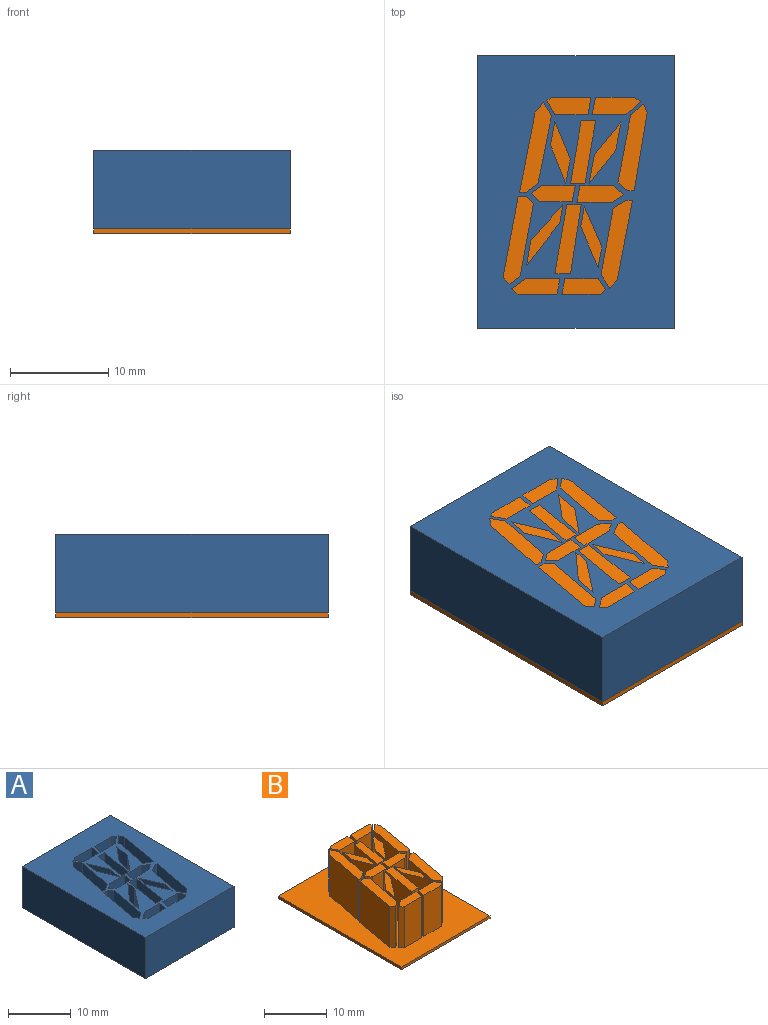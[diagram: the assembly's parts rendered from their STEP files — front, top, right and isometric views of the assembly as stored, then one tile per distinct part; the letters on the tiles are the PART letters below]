
ASSEMBLY  parts=2 mates=1
PART A: 84 faces, bbox 20x27.7x8 mm
  f0: plane 8x3.38mm, normal (0,1,0), area 27mm2, adj f1,f81,f82,f83
  f1: plane 8x1.47mm, normal (0.87,0.49,0), area 13.5mm2, adj f0,f2,f82,f83
  f2: plane 8x0.6mm, normal (0.49,-0.87,0), area 5.4mm2, adj f1,f3,f82,f83
  f3: plane 8x3.88mm, normal (0,-1,0), area 31mm2, adj f2,f81,f82,f83
  f4: plane 8x3.46mm, normal (0,1,0), area 27.6mm2, adj f5,f65,f82,f83
  f5: plane 8x1.8mm, normal (0.98,-0.2,0), area 14.7mm2, adj f4,f6,f82,f83
  f6: plane 8x3.86mm, normal (0,-1,0), area 30.9mm2, adj f5,f7,f82,f83
  f7: plane 8x0.69mm, normal (-0.51,-0.86,0), area 6.5mm2, adj f6,f65,f82,f83
  f8: plane 8x6.88mm, normal (0.98,-0.18,0), area 56mm2, adj f9,f66,f82,f83
  f9: plane 8x1.33mm, normal (0.64,-0.77,0), area 13.8mm2, adj f8,f10,f82,f83
  f10: plane 8x0.86mm, normal (-0.92,-0.38,0), area 7.4mm2, adj f9,f11,f82,f83
  f11: plane 8x7.96mm, normal (-0.99,0.16,0), area 64.6mm2, adj f10,f12,f82,f83
  f12: plane 8x0.66mm, normal (0,1,0), area 5.3mm2, adj f11,f66,f82,f83
  f13: plane 8x1.39mm, normal (0.84,0.54,0), area 13.3mm2, adj f14,f67,f82,f83
  f14: plane 8x6.77mm, normal (0.98,-0.18,0), area 55.1mm2, adj f13,f15,f82,f83
  f15: plane 8x1.39mm, normal (0.51,-0.86,0), area 12.8mm2, adj f14,f16,f82,f83
  f16: plane 8x0.57mm, normal (0,-1,0), area 4.6mm2, adj f15,f17,f82,f83
  f17: plane 8.08x8mm, normal (-0.98,0.19,0), area 65.8mm2, adj f16,f67,f82,f83
  f18: plane 8x3.87mm, normal (0,1,0), area 31mm2, adj f19,f68,f82,f83
  f19: plane 8x1.61mm, normal (0.98,-0.18,0), area 13.1mm2, adj f18,f20,f82,f83
  f20: plane 8x3.39mm, normal (0,-1,0), area 27.1mm2, adj f19,f21,f82,f83
  f21: plane 8x1.15mm, normal (-0.84,-0.54,0), area 11mm2, adj f20,f68,f82,f83
  f22: plane 8x1.6mm, normal (-0.98,0.19,0), area 13.1mm2, adj f23,f69,f82,f83
  f23: plane 8x3.94mm, normal (0,1,0), area 31.5mm2, adj f22,f24,f82,f83
  f24: plane 8x0.64mm, normal (0.65,0.76,0), area 6.7mm2, adj f23,f25,f82,f83
  f25: plane 8x1.43mm, normal (0.59,-0.81,0), area 14.2mm2, adj f24,f69,f82,f83
  f26: plane 8x1.13mm, normal (-0.63,0.78,0), area 11.6mm2, adj f27,f70,f82,f83
  f27: plane 8x0.69mm, normal (0.74,0.67,0), area 7.4mm2, adj f26,f28,f82,f83
  f28: plane 8.3x8mm, normal (0.98,-0.18,0), area 67.5mm2, adj f27,f29,f82,f83
  f29: plane 8x0.85mm, normal (0,-1,0), area 6.8mm2, adj f28,f30,f82,f83
  f30: plane 8x0.74mm, normal (-0.72,-0.69,0), area 8.2mm2, adj f29,f70,f82,f83
  f31: plane 8x1.47mm, normal (0,1,0), area 11.7mm2, adj f32,f71,f82,f83
  f32: plane 8x6.33mm, normal (0.99,-0.17,0), area 51.4mm2, adj f31,f33,f82,f83
  f33: plane 8x1.47mm, normal (0,-1,0), area 11.8mm2, adj f32,f71,f82,f83
  f34: plane 8x3.35mm, normal (-0.78,0.63,0), area 34.5mm2, adj f35,f72,f82,f83
  f35: plane 8x2.95mm, normal (0.98,-0.18,0), area 24mm2, adj f34,f36,f82,f83
  f36: plane 8x3.27mm, normal (0.77,-0.64,0), area 33.9mm2, adj f35,f72,f82,f83
  f37: plane 8x7.04mm, normal (0.99,-0.17,0), area 57.1mm2, adj f38,f73,f82,f83
  f38: plane 8x1.47mm, normal (0,-1,0), area 11.8mm2, adj f37,f39,f82,f83
  f39: plane 8x7.04mm, normal (-0.99,0.15,0), area 57mm2, adj f38,f73,f82,f83
  f40: plane 8x4.14mm, normal (0.92,0.39,0), area 36mm2, adj f41,f74,f82,f83
  f41: plane 8x2.04mm, normal (0.99,-0.17,0), area 16.5mm2, adj f40,f42,f82,f83
  f42: plane 8x4.1mm, normal (-0.92,-0.4,0), area 35.8mm2, adj f41,f74,f82,f83
  f43: plane 8x4.36mm, normal (-0.79,0.61,0), area 44.2mm2, adj f44,f75,f82,f83
  f44: plane 8x2.56mm, normal (0.99,-0.17,0), area 20.8mm2, adj f43,f45,f82,f83
  f45: plane 8x3.64mm, normal (0.74,-0.67,0), area 39.1mm2, adj f44,f75,f82,f83
  f46: plane 8x1.69mm, normal (0.98,-0.18,0), area 13.8mm2, adj f47,f76,f82,f83
  f47: plane 8x3.37mm, normal (0,-1,0), area 27mm2, adj f46,f48,f82,f83
  f48: plane 8x1.04mm, normal (-0.67,-0.74,0), area 11.2mm2, adj f47,f49,f82,f83
  f49: plane 8x1.14mm, normal (-0.56,0.83,0), area 10.9mm2, adj f48,f76,f82,f83
  f50: plane 8x3.42mm, normal (0,-1,0), area 27.3mm2, adj f51,f77,f82,f83
  f51: plane 8x1.65mm, normal (-0.98,0.19,0), area 13.5mm2, adj f50,f52,f82,f83
  f52: plane 8x3.28mm, normal (0,1,0), area 26.2mm2, adj f51,f53,f82,f83
  f53: plane 8x0.89mm, normal (0.72,0.69,0), area 9.8mm2, adj f52,f77,f82,f83
  f54: plane 8x2.47mm, normal (-0.98,0.18,0), area 20.1mm2, adj f55,f78,f82,f83
  f55: plane 8x3.89mm, normal (0.93,0.37,0), area 33.5mm2, adj f54,f56,f82,f83
  f56: plane 8x2.35mm, normal (0.98,-0.18,0), area 19.1mm2, adj f55,f78,f82,f83
  f57: plane 8x0.7mm, normal (0,1,0), area 5.6mm2, adj f58,f79,f82,f83
  f58: plane 8.03x8mm, normal (0.98,-0.19,0), area 65.4mm2, adj f57,f59,f82,f83
  f59: plane 8x1.1mm, normal (0.78,-0.62,0), area 11.2mm2, adj f58,f60,f82,f83
  f60: plane 8x1.39mm, normal (-0.86,-0.51,0), area 12.9mm2, adj f59,f61,f82,f83
  f61: plane 8x6.9mm, normal (-0.98,0.2,0), area 56.3mm2, adj f60,f79,f82,f83
  f62: plane 27.7x8mm, normal (-1,0,0), area 221.6mm2, adj f63,f80,f82,f83
  f63: plane 20x8mm, normal (0,-1,0), area 160mm2, adj f62,f64,f82,f83
  f64: plane 27.7x8mm, normal (1,0,0), area 221.6mm2, adj f63,f80,f82,f83
  f65: plane 8x1.47mm, normal (-0.69,0.73,0), area 16.1mm2, adj f4,f7,f82,f83
  f66: plane 8x1mm, normal (0.64,0.77,0), area 10.4mm2, adj f8,f12,f82,f83
  f67: plane 8x0.9mm, normal (-0.77,0.64,0), area 9.4mm2, adj f13,f17,f82,f83
  f68: plane 8x0.55mm, normal (-0.64,0.77,0), area 5.8mm2, adj f18,f21,f82,f83
  f69: plane 8x3.47mm, normal (0,-1,0), area 27.8mm2, adj f22,f25,f82,f83
  f70: plane 8x7.33mm, normal (-0.98,0.18,0), area 59.6mm2, adj f26,f30,f82,f83
  f71: plane 8x6.33mm, normal (-0.99,0.17,0), area 51.4mm2, adj f31,f33,f82,f83
  f72: plane 8x2.87mm, normal (-0.98,0.18,0), area 23.4mm2, adj f34,f36,f82,f83
  f73: plane 8x1.6mm, normal (0,1,0), area 12.8mm2, adj f37,f39,f82,f83
  f74: plane 8x2.08mm, normal (-0.98,0.18,0), area 16.9mm2, adj f40,f42,f82,f83
  f75: plane 8x1.83mm, normal (-0.99,0.17,0), area 14.9mm2, adj f43,f45,f82,f83
  f76: plane 8x3.59mm, normal (0,1,0), area 28.7mm2, adj f46,f49,f82,f83
  f77: plane 8x1.03mm, normal (0.6,-0.8,0), area 10.2mm2, adj f50,f53,f82,f83
  f78: plane 8x3.77mm, normal (-0.92,-0.38,0), area 32.6mm2, adj f54,f56,f82,f83
  f79: plane 8x1.17mm, normal (-0.58,0.81,0), area 11.5mm2, adj f57,f61,f82,f83
  f80: plane 20x8mm, normal (0,1,0), area 160mm2, adj f62,f64,f82,f83
  f81: plane 8x1.8mm, normal (-0.99,0.15,0), area 14.6mm2, adj f0,f3,f82,f83
  f82: plane 27.7x20mm, normal (0,0,1), area 414.1mm2, adj f0,f1,f2,f3,f4,f5,f6,f7
  f83: plane 27.7x20mm, normal (0,0,-1), area 414.1mm2, adj f0,f1,f2,f3,f4,f5,f6,f7
PART B: 100 faces, bbox 20x27.7x8.5 mm
  f0: plane 27.7x20mm, normal (0,0,1), area 414.1mm2, adj f1,f2,f3,f4,f6,f7,f8,f9
  f1: plane 27.7x0.5mm, normal (-1,0,0), area 13.8mm2, adj f0,f2,f4,f5
  f2: plane 20x0.5mm, normal (0,-1,0), area 10mm2, adj f0,f1,f3,f5
  f3: plane 27.7x0.5mm, normal (1,0,0), area 13.8mm2, adj f0,f2,f4,f5
  f4: plane 20x0.5mm, normal (0,1,0), area 10mm2, adj f0,f1,f3,f5
  f5: plane 27.7x20mm, normal (0,0,-1), area 554mm2, adj f1,f2,f3,f4
  f6: plane 8x1.47mm, normal (-0.87,-0.49,0), area 13.5mm2, adj f0,f7,f10,f11
  f7: plane 8x3.38mm, normal (0,-1,0), area 27mm2, adj f0,f6,f8,f11
  f8: plane 8x1.8mm, normal (0.99,-0.15,0), area 14.6mm2, adj f0,f7,f9,f11
  f9: plane 8x3.88mm, normal (0,1,0), area 31mm2, adj f0,f8,f10,f11
  f10: plane 8x0.6mm, normal (-0.49,0.87,0), area 5.4mm2, adj f0,f6,f9,f11
  f11: plane 4.47x1.8mm, normal (0,0,1), area 7.1mm2, adj f6,f7,f8,f9,f10
  f12: plane 8x1.8mm, normal (-0.98,0.2,0), area 14.7mm2, adj f0,f13,f16,f17
  f13: plane 8x3.46mm, normal (0,-1,0), area 27.6mm2, adj f0,f12,f14,f17
  f14: plane 8x1.47mm, normal (0.69,-0.73,0), area 16.1mm2, adj f0,f13,f15,f17
  f15: plane 8x0.69mm, normal (0.51,0.86,0), area 6.5mm2, adj f0,f14,f16,f17
  f16: plane 8x3.86mm, normal (0,1,0), area 30.9mm2, adj f0,f12,f15,f17
  f17: plane 4.92x1.8mm, normal (0,0,1), area 7.4mm2, adj f12,f13,f14,f15,f16
  f18: plane 8x1.33mm, normal (-0.64,0.77,0), area 13.8mm2, adj f0,f19,f23,f24
  f19: plane 8x6.88mm, normal (-0.98,0.18,0), area 56mm2, adj f0,f18,f20,f24
  f20: plane 8x1mm, normal (-0.64,-0.77,0), area 10.4mm2, adj f0,f19,f21,f24
  f21: plane 8x0.66mm, normal (0,-1,0), area 5.3mm2, adj f0,f20,f22,f24
  f22: plane 8x7.96mm, normal (0.99,-0.16,0), area 64.6mm2, adj f0,f21,f23,f24
  f23: plane 8x0.86mm, normal (0.92,0.38,0), area 7.4mm2, adj f0,f18,f22,f24
  f24: plane 8.82x2.98mm, normal (0,0,1), area 13.8mm2, adj f18,f19,f20,f21,f22,f23
  f25: plane 8x6.77mm, normal (-0.98,0.18,0), area 55.1mm2, adj f0,f26,f30,f31
  f26: plane 8x1.39mm, normal (-0.84,-0.54,0), area 13.3mm2, adj f0,f25,f27,f31
  f27: plane 8x0.9mm, normal (0.77,-0.64,0), area 9.4mm2, adj f0,f26,f28,f31
  f28: plane 8.08x8mm, normal (0.98,-0.19,0), area 65.8mm2, adj f0,f27,f29,f31
  f29: plane 8x0.57mm, normal (0,1,0), area 4.6mm2, adj f0,f28,f30,f31
  f30: plane 8x1.39mm, normal (-0.51,0.86,0), area 12.8mm2, adj f0,f25,f29,f31
  f31: plane 8.98x3.19mm, normal (0,0,1), area 14.4mm2, adj f25,f26,f27,f28,f29,f30
  f32: plane 8x1.61mm, normal (-0.98,0.18,0), area 13.1mm2, adj f0,f33,f36,f37
  f33: plane 8x3.87mm, normal (0,-1,0), area 31mm2, adj f0,f32,f34,f37
  f34: plane 8x0.55mm, normal (0.64,-0.77,0), area 5.8mm2, adj f0,f33,f35,f37
  f35: plane 8x1.15mm, normal (0.84,0.54,0), area 11mm2, adj f0,f34,f36,f37
  f36: plane 8x3.39mm, normal (0,1,0), area 27.1mm2, adj f0,f32,f35,f37
  f37: plane 4.43x1.61mm, normal (0,0,1), area 6.4mm2, adj f32,f33,f34,f35,f36
  f38: plane 8x3.94mm, normal (0,-1,0), area 31.5mm2, adj f0,f39,f42,f43
  f39: plane 8x1.6mm, normal (0.98,-0.19,0), area 13.1mm2, adj f0,f38,f40,f43
  f40: plane 8x3.47mm, normal (0,1,0), area 27.8mm2, adj f0,f39,f41,f43
  f41: plane 8x1.43mm, normal (-0.59,0.81,0), area 14.2mm2, adj f0,f40,f42,f43
  f42: plane 8x0.64mm, normal (-0.65,-0.76,0), area 6.7mm2, adj f0,f38,f41,f43
  f43: plane 4.9x1.6mm, normal (0,0,1), area 6.7mm2, adj f38,f39,f40,f41,f42
  f44: plane 8x0.69mm, normal (-0.74,-0.67,0), area 7.4mm2, adj f0,f45,f49,f50
  f45: plane 8x1.13mm, normal (0.63,-0.78,0), area 11.6mm2, adj f0,f44,f46,f50
  f46: plane 8x7.33mm, normal (0.98,-0.18,0), area 59.6mm2, adj f0,f45,f47,f50
  f47: plane 8x0.74mm, normal (0.72,0.69,0), area 8.2mm2, adj f0,f46,f48,f50
  f48: plane 8x0.85mm, normal (0,1,0), area 6.8mm2, adj f0,f47,f49,f50
  f49: plane 8.3x8mm, normal (-0.98,0.18,0), area 67.5mm2, adj f0,f44,f48,f50
  f50: plane 8.98x3.09mm, normal (0,0,1), area 14.3mm2, adj f44,f45,f46,f47,f48,f49
  f51: plane 8.03x8mm, normal (-0.98,0.19,0), area 65.4mm2, adj f0,f52,f56,f57
  f52: plane 8x0.7mm, normal (0,-1,0), area 5.6mm2, adj f0,f51,f53,f57
  f53: plane 8x1.17mm, normal (0.58,-0.81,0), area 11.5mm2, adj f0,f52,f54,f57
  f54: plane 8x6.9mm, normal (0.98,-0.2,0), area 56.3mm2, adj f0,f53,f55,f57
  f55: plane 8x1.39mm, normal (0.86,0.51,0), area 12.9mm2, adj f0,f54,f56,f57
  f56: plane 8x1.1mm, normal (-0.78,0.62,0), area 11.2mm2, adj f0,f51,f55,f57
  f57: plane 9.12x3.25mm, normal (0,0,1), area 14.2mm2, adj f51,f52,f53,f54,f55,f56
  f58: plane 8x3.89mm, normal (-0.93,-0.37,0), area 33.5mm2, adj f0,f59,f61,f62
  f59: plane 8x2.47mm, normal (0.98,-0.18,0), area 20.1mm2, adj f0,f58,f60,f62
  f60: plane 8x3.77mm, normal (0.92,0.38,0), area 32.6mm2, adj f0,f59,f61,f62
  f61: plane 8x2.35mm, normal (-0.98,0.18,0), area 19.1mm2, adj f0,f58,f60,f62
  f62: plane 6.24x2mm, normal (0,0,1), area 5.4mm2, adj f58,f59,f60,f61
  f63: plane 8x6.33mm, normal (-0.99,0.17,0), area 51.4mm2, adj f0,f64,f66,f67
  f64: plane 8x1.47mm, normal (0,-1,0), area 11.7mm2, adj f0,f63,f65,f67
  f65: plane 8x6.33mm, normal (0.99,-0.17,0), area 51.4mm2, adj f0,f64,f66,f67
  f66: plane 8x1.47mm, normal (0,1,0), area 11.8mm2, adj f0,f63,f65,f67
  f67: plane 6.33x2.54mm, normal (0,0,1), area 9.3mm2, adj f63,f64,f65,f66
  f68: plane 8x2.95mm, normal (-0.98,0.18,0), area 24mm2, adj f0,f69,f71,f72
  f69: plane 8x3.35mm, normal (0.78,-0.63,0), area 34.5mm2, adj f0,f68,f70,f72
  f70: plane 8x2.87mm, normal (0.98,-0.18,0), area 23.4mm2, adj f0,f69,f71,f72
  f71: plane 8x3.27mm, normal (-0.77,0.64,0), area 33.9mm2, adj f0,f68,f70,f72
  f72: plane 6.23x3.25mm, normal (0,0,1), area 6.1mm2, adj f68,f69,f70,f71
  f73: plane 8x1.65mm, normal (0.98,-0.19,0), area 13.5mm2, adj f0,f74,f77,f78
  f74: plane 8x3.42mm, normal (0,1,0), area 27.3mm2, adj f0,f73,f75,f78
  f75: plane 8x1.03mm, normal (-0.6,0.8,0), area 10.2mm2, adj f0,f74,f76,f78
  f76: plane 8x0.89mm, normal (-0.72,-0.69,0), area 9.8mm2, adj f0,f75,f77,f78
  f77: plane 8x3.28mm, normal (0,-1,0), area 26.2mm2, adj f0,f73,f76,f78
  f78: plane 4.44x1.65mm, normal (0,0,1), area 6.3mm2, adj f73,f74,f75,f76,f77
  f79: plane 8x3.37mm, normal (0,1,0), area 27mm2, adj f0,f80,f83,f84
  f80: plane 8x1.69mm, normal (-0.98,0.18,0), area 13.8mm2, adj f0,f79,f81,f84
  f81: plane 8x3.59mm, normal (0,-1,0), area 28.7mm2, adj f0,f80,f82,f84
  f82: plane 8x1.14mm, normal (0.56,-0.83,0), area 10.9mm2, adj f0,f81,f83,f84
  f83: plane 8x1.04mm, normal (0.67,0.74,0), area 11.2mm2, adj f0,f79,f82,f84
  f84: plane 4.72x1.69mm, normal (0,0,1), area 6.8mm2, adj f79,f80,f81,f82,f83
  f85: plane 8x1.47mm, normal (0,1,0), area 11.8mm2, adj f0,f86,f88,f89
  f86: plane 8x7.04mm, normal (-0.99,0.17,0), area 57.1mm2, adj f0,f85,f87,f89
  f87: plane 8x1.6mm, normal (0,-1,0), area 12.8mm2, adj f0,f86,f88,f89
  f88: plane 8x7.04mm, normal (0.99,-0.15,0), area 57mm2, adj f0,f85,f87,f89
  f89: plane 7.04x2.69mm, normal (0,0,1), area 10.8mm2, adj f85,f86,f87,f88
  f90: plane 8x2.04mm, normal (-0.99,0.17,0), area 16.5mm2, adj f0,f91,f93,f94
  f91: plane 8x4.14mm, normal (-0.92,-0.39,0), area 36mm2, adj f0,f90,f92,f94
  f92: plane 8x2.08mm, normal (0.98,-0.18,0), area 16.9mm2, adj f0,f91,f93,f94
  f93: plane 8x4.1mm, normal (0.92,0.4,0), area 35.8mm2, adj f0,f90,f92,f94
  f94: plane 6.18x2.13mm, normal (0,0,1), area 5.1mm2, adj f90,f91,f92,f93
  f95: plane 8x2.56mm, normal (-0.99,0.17,0), area 20.8mm2, adj f0,f96,f98,f99
  f96: plane 8x4.36mm, normal (0.79,-0.61,0), area 44.2mm2, adj f0,f95,f97,f99
  f97: plane 8x1.83mm, normal (0.99,-0.17,0), area 14.9mm2, adj f0,f96,f98,f99
  f98: plane 8x3.64mm, normal (-0.74,0.67,0), area 39.1mm2, adj f0,f95,f97,f99
  f99: plane 6.19x3.7mm, normal (0,0,1), area 5.8mm2, adj f95,f96,f97,f98
PLACE A t=(-36.34,-4.92,12.67)mm
PLACE B t=(-36.34,-4.92,12.67)mm
MATE fastened B.f0 <-> A.f83  axis (0,0,1) through (-36.34,22.78,13.17)mm
